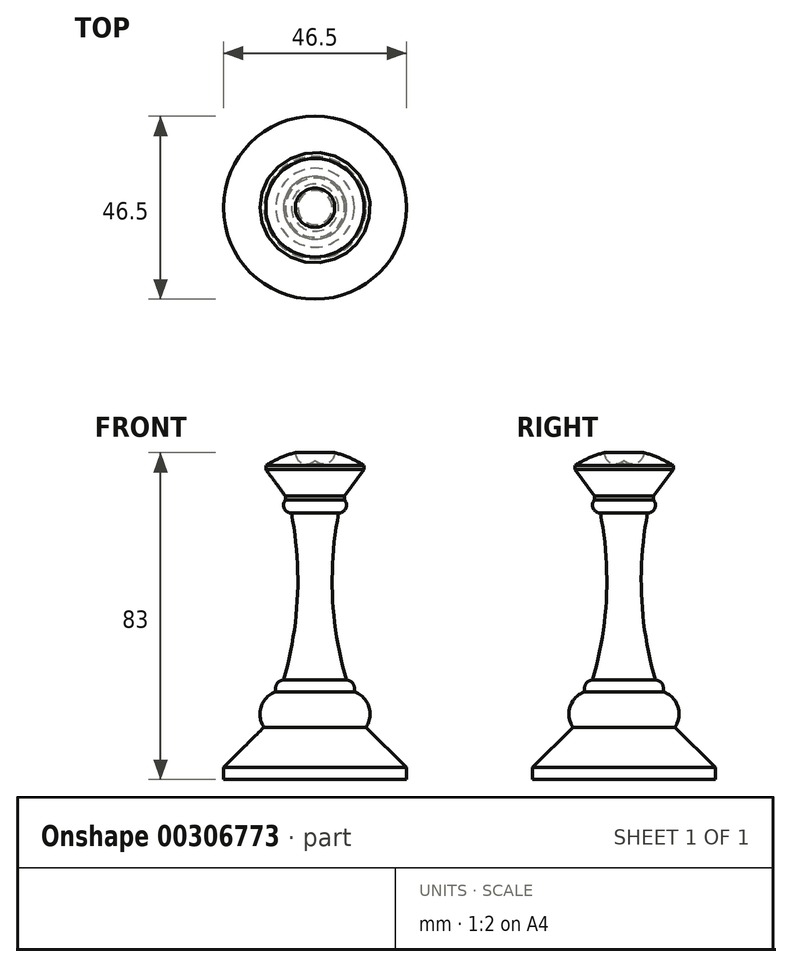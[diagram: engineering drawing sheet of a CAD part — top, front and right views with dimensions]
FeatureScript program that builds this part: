
annotation { "Feature Type Name" : "Feature", "Feature Type Description" : "" }
export const myFeature = defineFeature(function(context is Context, id is Id, definition is map)
    precondition{}
    {
        {
            var Q0;
            Q0=qCreatedBy(makeId("Front.planeOp"),FACE);
            var sketch = newSketch(context, id + "F0", { "sketchPlane" : qUnion([Q0])});
            skLineSegment(sketch, "E0", {"start": v(0, -210.74) * mm, "end": v(0, 0) * mm});
            skArc(sketch, "E1", {"start": v(6, -17.35) * mm, "mid": v(7.82, -16.17) * mm, "end": v(7.5, -14.02) * mm});
            skArc(sketch, "E2", {"start": v(6, -17.35) * mm, "mid": v(4.46, -38.68) * mm, "end": v(8, -59.78) * mm});
            skLineSegment(sketch, "E3", {"start": v(10, -61.78) * mm, "end": v(10, -62.78) * mm});
            skArc(sketch, "E4", {"start": v(13, -71.75) * mm, "mid": v(13.7, -66.53) * mm, "end": v(10, -62.78) * mm});
            skLineSegment(sketch, "E5", {"start": v(23.25, -82) * mm, "end": v(23.25, -85) * mm});
            skLineSegment(sketch, "E6", {"start": v(23.25, -85) * mm, "end": v(0, -85) * mm});
            skLineSegment(sketch, "E7", {"start": v(0, -85) * mm, "end": v(0, 0) * mm, "construction": true});
            skLineSegment(sketch, "E8", {"start": v(0, -82) * mm, "end": v(32.4, -82) * mm, "construction": true});
            skArc(sketch, "E9", {"start": v(5, -2) * mm, "mid": v(3.18, 0.7) * mm, "end": v(0, 0) * mm});
            skArc(sketch, "E10", {"start": v(12.5, -5.27) * mm, "mid": v(8.88, -3.33) * mm, "end": v(5, -2) * mm});
            skLineSegment(sketch, "E11", {"start": v(12.5, -5.27) * mm, "end": v(12.5, -6.27) * mm});
            skLineSegment(sketch, "E12", {"start": v(12.5, -6.27) * mm, "end": v(7.5, -13.02) * mm});
            skLineSegment(sketch, "E13", {"start": v(7.5, -14.02) * mm, "end": v(7.5, -13.02) * mm});
            skLineSegment(sketch, "E14", {"start": v(13, -71.75) * mm, "end": v(23.25, -82) * mm});
            skArc(sketch, "E15", {"start": v(10, -61.78) * mm, "mid": v(9.41, -60.36) * mm, "end": v(8, -59.78) * mm});
            skSolve(sketch);
        }
        {
            var Q0;
            Q0=makeQuery(id+"F0.imprint","IMPRINT",FACE,{"disambiguationData":[TD([[makeQuery(id+"F0.imprint","IMPRINT",EDGE,{"derivedFrom":sQuery(id+"F0.wireOp",EDGE,"E1")}),1.0]])]});
            var Q1;
            Q1=sQuery(id+"F0.wireOp",EDGE,"E0");
            revolve(context, id + "F1", {"entities" : qUnion([Q0]), "axis" : qUnion([Q1]), "revolveType" : RevolveType.FULL});
        }
    });
